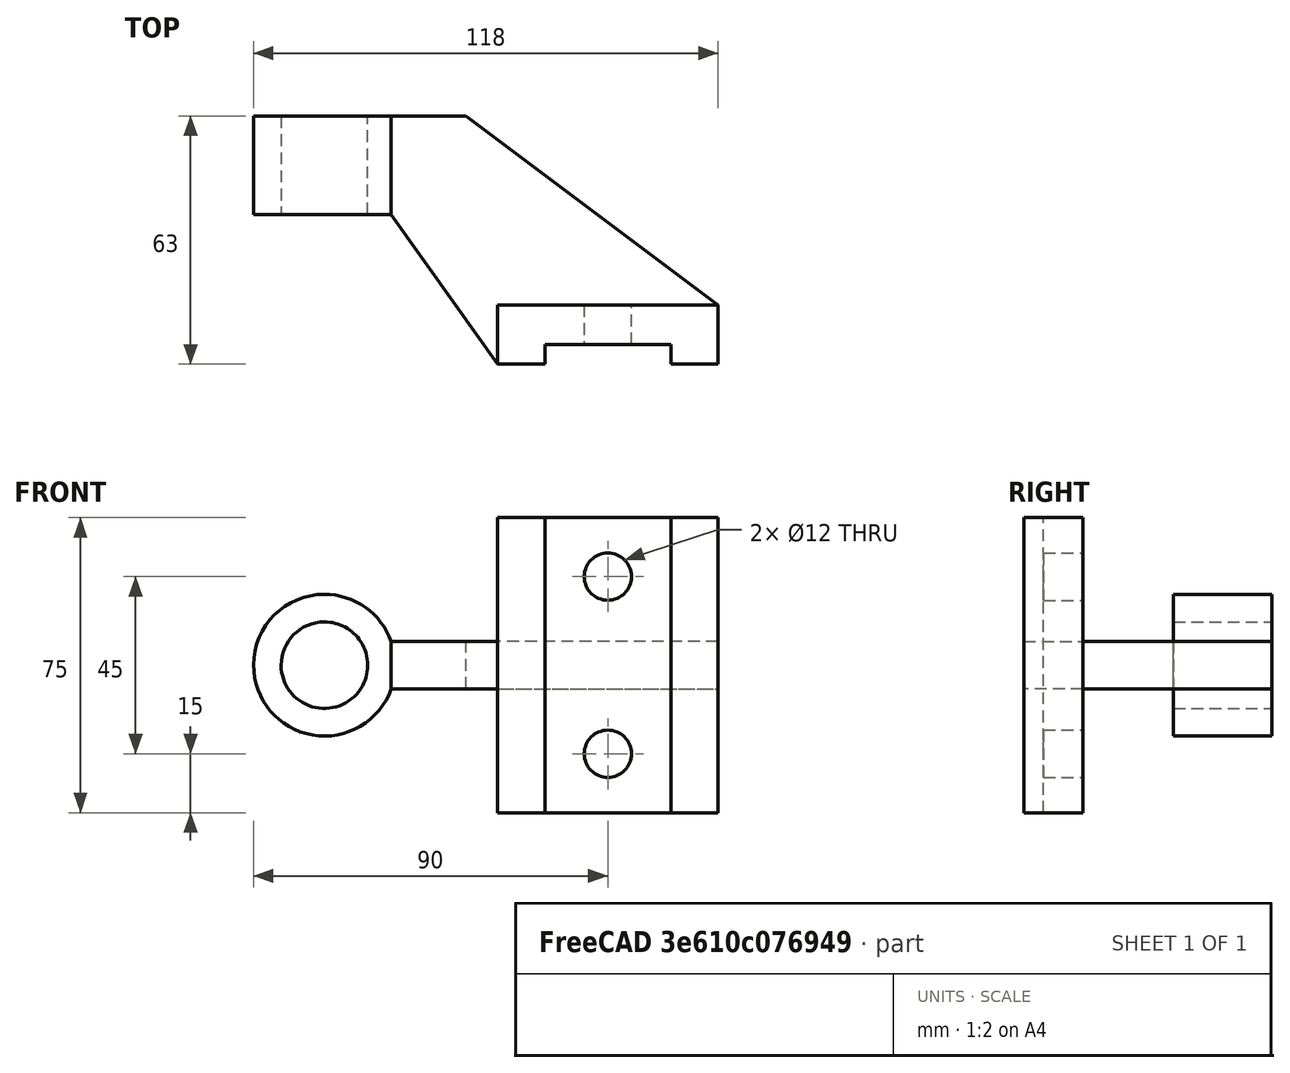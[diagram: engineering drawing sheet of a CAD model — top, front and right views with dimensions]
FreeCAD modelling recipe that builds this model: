
FCSTD DOCUMENT  (FreeCAD 0.18R4 (GitTag))
Label: Ass2 2nd sem
License: All rights reserved
LicenseURL: http://en.wikipedia.org/wiki/All_rights_reserved
objects: TechDraw::DrawViewDimension×15, Sketcher::SketchObject×9, TechDraw::DrawProjGroup×6, PartDesign::Pad×4, PartDesign::Pocket×4, TechDraw::DrawViewAnnotation×3, TechDraw::DrawProjGroupItem×3, TechDraw::DrawSVGTemplate×1, PartDesign::Body×1, TechDraw::DrawPage×1
note: 26 computed .brp shape members not serialized (recipe doc carries the construction recipe); baked Part::Feature solids carry a one-line shape summary decoded from their .brp

FEATURE [Sketcher::SketchObject] Sketch
  MapMode = 5
  Support = -> [XY_Plane]
  sketch-geometry (8):
    g0: LineSegment StartX=-28 StartY=-5.85e-14 StartZ=0 EndX=-28 EndY=15 EndZ=0
    g1: LineSegment StartX=-28 StartY=15 StartZ=0 EndX=28 EndY=15 EndZ=0
    g2: LineSegment StartX=28 StartY=15 StartZ=0 EndX=28 EndY=5.86e-14 EndZ=0
    g3: LineSegment StartX=28 StartY=5.86e-14 StartZ=0 EndX=16 EndY=0 EndZ=0
    g4: LineSegment StartX=16 StartY=0 StartZ=0 EndX=16 EndY=5 EndZ=0
    g5: LineSegment StartX=16 StartY=5 StartZ=0 EndX=-16 EndY=5 EndZ=0
    g6: LineSegment StartX=-16 StartY=5 StartZ=0 EndX=-16 EndY=0 EndZ=0
    g7: LineSegment StartX=-16 StartY=-1e-16 StartZ=0 EndX=-28 EndY=-5.85e-14 EndZ=0
  constraints (23):
    c: Coincident(g0,g1)
    c: Coincident(g1,g2)
    c: Coincident(g2,g3)
    c: Coincident(g3,g4)
    c: Coincident(g4,g5)
    c: Coincident(g5,g6)
    c: Coincident(g6,g7)
    c: Coincident(g7,g0)
    c: Parallel(g7,g3)
    c: Parallel(g3,g5)
    c: Parallel(g5,g1)
    c: DistanceX(g7,g7) = 12
    c: DistanceX(g3,g3) = 12
    c: Parallel(g6,g0)
    c: Parallel(g0,g4)
    c: Parallel(g4,g2)
    c: Parallel(g2,g-2)
    c: DistanceY(g4,g4) = 5
    c: DistanceY(g6,g6) = 5
    c: DistanceY(g2,g2) = 15
    c: Symmetric(g0,g1,g-2)
    c: DistanceX(g1,g1) = 56
    c: PointOnObject(g3,g-1)
FEATURE [PartDesign::Pad] Pad
  Length = 75
  Length2 = 100
  Midplane = true
  Profile = -> Sketch
  Type = 0
FEATURE [Sketcher::SketchObject] Sketch001
  ExternalGeometry = -> [Pad]
  MapMode = 5
  Placement = pos=(0,15,0) rot=(0,0.707107,0.707107;3.14159rad)
  Support = -> [Pad]
  sketch-geometry (4):
    g0: LineSegment StartX=-28 StartY=6 StartZ=0 EndX=72 EndY=6 EndZ=0
    g1: LineSegment StartX=72 StartY=6 StartZ=0 EndX=72 EndY=-6 EndZ=0
    g2: LineSegment StartX=72 StartY=-6 StartZ=0 EndX=-28 EndY=-6 EndZ=0
    g3: LineSegment StartX=-28 StartY=-6 StartZ=0 EndX=-28 EndY=6 EndZ=0
  constraints (11):
    c: Coincident(g0,g1)
    c: Coincident(g1,g2)
    c: Coincident(g2,g3)
    c: Coincident(g3,g0)
    c: Horizontal(g0)
    c: Horizontal(g2)
    c: Vertical(g1)
    c: DistanceY(g3,g3) = 12
    c: PointOnObject(g0,g-3)
    c: Symmetric(g0,g2,g-1)
    c: DistanceX(g0,g0) = 100
FEATURE [PartDesign::Pad] Pad001
  BaseFeature = -> Pad
  Length = 48
  Length2 = 100
  Profile = -> Sketch001
  Type = 0
FEATURE [Sketcher::SketchObject] Sketch002
  ExternalGeometry = -> [Pad001]
  MapMode = 5
  Placement = pos=(0,15,-4.5e-15) rot=(1,0,0;1.5708rad)
  Support = -> [Pad001]
  sketch-geometry (4):
    g0: LineSegment StartX=-28 StartY=6 StartZ=0 EndX=-72 EndY=6 EndZ=0
    g1: LineSegment StartX=-72 StartY=6 StartZ=0 EndX=-72 EndY=-6 EndZ=0
    g2: LineSegment StartX=-72 StartY=-6 StartZ=0 EndX=-28 EndY=-6 EndZ=0
    g3: LineSegment StartX=-28 StartY=-6 StartZ=0 EndX=-28 EndY=6 EndZ=0
  constraints (9):
    c: Coincident(g0,g1)
    c: Coincident(g1,g2)
    c: Coincident(g2,g3)
    c: Coincident(g3,g0)
    c: Horizontal(g2)
    c: Vertical(g1)
    c: Coincident(g2,g-5)
    c: Coincident(g0,g-3)
    c: Coincident(g-3,g0)
FEATURE [PartDesign::Pad] Pad002
  BaseFeature = -> Pad001
  Length = 15
  Length2 = 100
  Profile = -> Sketch002
  Type = 0
FEATURE [Sketcher::SketchObject] Sketch003
  MapMode = 5
  Placement = pos=(0,-1.3e-15,-6) rot=(1,0,0;3.14159rad)
  Support = -> [Pad002]
FEATURE [Sketcher::SketchObject] Sketch004
  ExternalGeometry = -> [Pad002]
  MapMode = 5
  Placement = pos=(0,-1.3e-15,-6) rot=(1,0,0;3.14159rad)
  Support = -> [Pad002]
  sketch-geometry (6):
    g0: LineSegment StartX=-36 StartY=-63 StartZ=0 EndX=28 EndY=-15 EndZ=0
    g1: LineSegment StartX=28 StartY=-15 StartZ=0 EndX=28 EndY=-63 EndZ=0
    g2: LineSegment StartX=28 StartY=-63 StartZ=0 EndX=-36 EndY=-63 EndZ=0
    g3: LineSegment StartX=-72 StartY=-38 StartZ=0 EndX=-28 EndY=4.97e-14 EndZ=0
    g4: LineSegment StartX=-28 StartY=4.97e-14 StartZ=0 EndX=-72 EndY=-5.86e-14 EndZ=0
    g5: LineSegment StartX=-72 StartY=-5.86e-14 StartZ=0 EndX=-72 EndY=-38 EndZ=0
  constraints (10):
    c: Coincident(g0,g1)
    c: Coincident(g1,g2)
    c: Coincident(g2,g0)
    c: Coincident(g1,g-3)
    c: Coincident(g0,g-5)
    c: Coincident(g3,g4)
    c: Coincident(g4,g5)
    c: Coincident(g5,g3)
    c: Coincident(g4,g-7)
    c: Coincident(g3,g-6)
FEATURE [PartDesign::Pocket] Pocket
  BaseFeature = -> Pad002
  Length = 5
  Length2 = 100
  Profile = -> Sketch004
  Type = 1
FEATURE [Sketcher::SketchObject] Sketch005
  ExternalGeometry = -> [Pocket]
  MapMode = 5
  Placement = pos=(0,63,-1.89e-14) rot=(0,0.707107,0.707107;3.14159rad)
  Support = -> [Pocket]
  sketch-geometry (2):
    g0: Circle CenterX=72 CenterY=0 CenterZ=0 NormalX=0 NormalY=0 NormalZ=1 AngleXU=0 Radius=18
    g1: Circle CenterX=72 CenterY=0 CenterZ=0 NormalX=0 NormalY=0 NormalZ=1 AngleXU=0 Radius=11
  constraints (5):
    c: Radius(g0) = 18
    c: PointOnObject(g0,g-3)
    c: PointOnObject(g0,g-1)
    c: Radius(g1) = 11
    c: Coincident(g1,g0)
FEATURE [Sketcher::SketchObject] Sketch007
  MapMode = 5
  Placement = pos=(0,15,0) rot=(0,0.707107,0.707107;3.14159rad)
  sketch-geometry (2):
    g0: Circle CenterX=0 CenterY=22.5 CenterZ=0 NormalX=0 NormalY=0 NormalZ=1 AngleXU=0 Radius=6
    g1: Circle CenterX=0 CenterY=-22.5 CenterZ=0 NormalX=0 NormalY=0 NormalZ=1 AngleXU=0 Radius=6
  constraints (5):
    c: PointOnObject(g1,g-2)
    c: PointOnObject(g0,g-2)
    c: Radius(g0) = 6
    c: Radius(g1) = 6
    c: DistanceY(g1,g0) = 45
FEATURE [PartDesign::Pocket] Pocket002
  BaseFeature = -> Pocket
  Length = 5
  Length2 = 100
  Profile = -> Sketch007
  Type = 1
FEATURE [TechDraw::DrawSVGTemplate] Template
  EditableTexts = Designed_by_Name=Soumojit Shome; Drawing_number=Assignment 2; FC-Date=21/04/2023; FC-SC=1:1; FC-SH=02; FC-Title=Academy of Technology; Subtitle=ECE2 (Y) 16900322101; Weight=Weight
  Height = 210
  Orientation = 1
  Width = 297
FEATURE [TechDraw::DrawProjGroup] ProjGroup
  AutoDistribute = true
  LockPosition = false
  ProjectionType = 0
  Rotation = 0
  ScaleType = 0
  Source = -> [Pocket002]
  X = 87.9071
  Y = 164.348
  spacingX = 15
  spacingY = 15
FEATURE [TechDraw::DrawViewAnnotation] Annotation
  Font = osifont
  LineSpace = 80
  LockPosition = false
  MaxWidth = -1
  Rotation = 0
  ScaleType = 0
  Text = Front View
  TextSize = 8
  TextStyle = 0
  X = 139.37
  Y = 143.597
FEATURE [TechDraw::DrawProjGroup] ProjGroup001
  AutoDistribute = true
  LockPosition = false
  ProjectionType = 0
  Rotation = 0
  ScaleType = 0
  Source = -> [Pocket002]
  X = 87.9071
  Y = 82.1739
  spacingX = 15
  spacingY = 15
FEATURE [TechDraw::DrawProjGroup] ProjGroup002
  AutoDistribute = true
  LockPosition = false
  ProjectionType = 0
  Rotation = 0
  ScaleType = 0
  Source = -> [Pocket002]
  X = 221.958
  Y = 135.296
  spacingX = 15
  spacingY = 15
FEATURE [TechDraw::DrawViewAnnotation] Annotation001
  Font = osifont
  LineSpace = 80
  LockPosition = false
  MaxWidth = -1
  Rotation = 0
  ScaleType = 0
  Text = Top View
  TextSize = 8
  TextStyle = 0
  X = 91.2273
  Y = 19.0909
FEATURE [TechDraw::DrawViewAnnotation] Annotation002
  Font = osifont
  LineSpace = 80
  LockPosition = false
  MaxWidth = -1
  Rotation = 0
  ScaleType = 0
  Text = Isometric View
  TextSize = 8
  TextStyle = 0
  X = 226.109
  Y = 70.9684
FEATURE [PartDesign::Pad] Pad003
  BaseFeature = -> Pocket002
  Length = 25
  Length2 = 100
  Profile = -> Sketch005
  Reversed = true
  Type = 0
FEATURE [Sketcher::SketchObject] Sketch008
  ExternalGeometry = -> [Pad003]
  MapMode = 5
  Placement = pos=(0,-1.3e-15,-6) rot=(1,0,0;3.14159rad)
  Support = -> [Pad003]
  sketch-geometry (3):
    g0: LineSegment StartX=-28 StartY=4.97e-14 StartZ=0 EndX=-55.0294 EndY=-38 EndZ=0
    g1: LineSegment StartX=-55.0294 StartY=-38 StartZ=0 EndX=-72 EndY=-38 EndZ=0
    g2: LineSegment StartX=-72 StartY=-38 StartZ=0 EndX=-28 EndY=4.97e-14 EndZ=0
  constraints (6):
    c: Coincident(g0,g1)
    c: Coincident(g1,g2)
    c: Coincident(g2,g0)
    c: Coincident(g2,g-4)
    c: Coincident(g0,g-3)
    c: Coincident(g1,g-5)
FEATURE [PartDesign::Pocket] Pocket003
  BaseFeature = -> Pad003
  Length = 5
  Length2 = 100
  Profile = -> Sketch008
  Type = 1
FEATURE [Sketcher::SketchObject] Sketch009
  ExternalGeometry = -> [Pocket003]
  MapMode = 5
  Placement = pos=(0,63,-1.89e-14) rot=(0,0.707107,0.707107;3.14159rad)
  Support = -> [Pocket003]
  sketch-geometry (4):
    g0: ArcOfCircle CenterX=72 CenterY=-8e-16 CenterZ=0 NormalX=0 NormalY=0 NormalZ=1 AngleXU=0 Radius=11 StartAngle=2.56466 EndAngle=3.71852
    g1: LineSegment StartX=62.7805 StartY=6 StartZ=0 EndX=72 EndY=6 EndZ=0
    g2: LineSegment StartX=72 StartY=6 StartZ=0 EndX=72 EndY=-6 EndZ=0
    g3: LineSegment StartX=72 StartY=-6 StartZ=0 EndX=62.7805 EndY=-6 EndZ=0
  constraints (9):
    c: Coincident(g0,g-3)
    c: Coincident(g0,g-3)
    c: Coincident(g0,g-3)
    c: Coincident(g1,g2)
    c: Coincident(g2,g3)
    c: Coincident(g3,g0)
    c: Coincident(g1,g0)
    c: Coincident(g1,g-4)
    c: Coincident(g-4,g2)
FEATURE [PartDesign::Pocket] Pocket004
  BaseFeature = -> Pocket003
  Length = 5
  Length2 = 100
  Profile = -> Sketch009
  Type = 1
FEATURE [PartDesign::Body] Body
  Group = -> [Sketch,Pad,Sketch001,Pad001,Sketch002,Pad002,Sketch003,Sketch004,Pocket,Sketch005,Sketch007,Pocket002,Pad003,Sketch008,Pocket003,Sketch009,Pocket004]
  Origin = -> Origin
  Tip = -> Pocket004
FEATURE [TechDraw::DrawProjGroupItem] ProjItem  label="Front"
  CoarseView = false
  Direction = (0,0,-1)
  Focus = 100
  HardHidden = false
  IsoCount = 0
  IsoHidden = false
  IsoVisible = false
  LockPosition = true
  Perspective = false
  Rotation = 0
  RotationVector = (-1,0,0)
  ScaleType = 2
  SeamHidden = false
  SeamVisible = false
  SmoothHidden = false
  SmoothVisible = false
  Source = -> [Pocket004]
  Type = 0
  X = 0
  Y = 0
FEATURE [TechDraw::DrawProjGroup] ProjGroup003
  Anchor = -> ProjItem
  AutoDistribute = true
  LockPosition = false
  ProjectionType = 0
  Rotation = 0
  ScaleType = 0
  Source = -> [Pocket004]
  Views = -> [ProjItem]
  X = 86.247
  Y = 164.763
  spacingX = 15
  spacingY = 15
FEATURE [TechDraw::DrawProjGroupItem] ProjItem001  label="Front001"
  CoarseView = false
  Direction = (0,1,0)
  Focus = 100
  HardHidden = false
  IsoCount = 0
  IsoHidden = false
  IsoVisible = false
  LockPosition = true
  Perspective = false
  Rotation = 0
  RotationVector = (-1,0,0)
  ScaleType = 2
  SeamHidden = false
  SeamVisible = false
  SmoothHidden = false
  SmoothVisible = false
  Source = -> [Pocket004]
  Type = 0
  X = 0
  Y = 0
FEATURE [TechDraw::DrawProjGroup] ProjGroup004
  Anchor = -> ProjItem001
  AutoDistribute = true
  LockPosition = false
  ProjectionType = 0
  Rotation = 0
  ScaleType = 0
  Source = -> [Pocket004]
  Views = -> [ProjItem001]
  X = 94.5474
  Y = 73.8735
  spacingX = 15
  spacingY = 15
FEATURE [TechDraw::DrawProjGroupItem] ProjItem002  label="Front002"
  CoarseView = false
  Direction = (0.715,0.437,-0.546)
  Focus = 100
  HardHidden = false
  IsoCount = 0
  IsoHidden = false
  IsoVisible = false
  LockPosition = true
  Perspective = false
  Rotation = 0
  RotationVector = (-0.623,0.042,-0.781)
  ScaleType = 2
  SeamHidden = false
  SeamVisible = false
  SmoothHidden = false
  SmoothVisible = false
  Source = -> [Pocket004]
  Type = 0
  X = 0
  Y = 0
FEATURE [TechDraw::DrawProjGroup] ProjGroup005
  Anchor = -> ProjItem002
  AutoDistribute = true
  LockPosition = false
  ProjectionType = 0
  Rotation = 0
  ScaleType = 0
  Source = -> [Pocket004]
  Views = -> [ProjItem002]
  X = 215.318
  Y = 134.881
  spacingX = 15
  spacingY = 15
FEATURE [TechDraw::DrawViewDimension] Dimension
  Arbitrary = false
  FormatSpec = ⌀%.2f
  LockPosition = false
  MeasureType = 1
  OverTolerance = 0
  References2D = -> [ProjItem001]
  Rotation = 0
  ScaleType = 0
  Type = 5
  UnderTolerance = 0
  X = 26.9763
  Y = 34.8617
FEATURE [TechDraw::DrawViewDimension] Dimension001
  Arbitrary = false
  FormatSpec = ⌀%.2f
  LockPosition = false
  MeasureType = 1
  OverTolerance = 0
  References2D = -> [ProjItem001]
  Rotation = 0
  ScaleType = 0
  Type = 5
  UnderTolerance = 0
  X = 18.2609
  Y = 24.4862
FEATURE [TechDraw::DrawViewDimension] Dimension002
  Arbitrary = false
  FormatSpec = %.2f
  LockPosition = false
  MeasureType = 1
  OverTolerance = 0
  References2D = -> [ProjItem]
  Rotation = 0
  ScaleType = 0
  Type = 2
  UnderTolerance = 0
  X = 63.5652
  Y = 19
FEATURE [TechDraw::DrawViewDimension] Dimension003
  Arbitrary = false
  FormatSpec = %.2f
  LockPosition = false
  MeasureType = 1
  OverTolerance = 0
  References2D = -> [ProjItem001]
  Rotation = 0
  ScaleType = 0
  Type = 1
  UnderTolerance = 0
  X = 22.585
  Y = -22.5059
FEATURE [TechDraw::DrawViewDimension] Dimension004
  Arbitrary = false
  FormatSpec = %.2f
  LockPosition = false
  MeasureType = 1
  OverTolerance = 0
  References2D = -> [ProjItem001]
  Rotation = 0
  ScaleType = 0
  Type = 1
  UnderTolerance = 0
  X = -6.9249
  Y = -41.1818
FEATURE [TechDraw::DrawViewDimension] Dimension005
  Arbitrary = false
  FormatSpec = %.2f
  LockPosition = false
  MeasureType = 1
  OverTolerance = 0
  References2D = -> [ProjItem001]
  Rotation = 0
  ScaleType = 0
  Type = 1
  UnderTolerance = 0
  X = -45
  Y = -52.8261
FEATURE [TechDraw::DrawViewDimension] Dimension006
  Arbitrary = false
  FormatSpec = %.2f
  LockPosition = false
  MeasureType = 1
  OverTolerance = 0
  References2D = -> [ProjItem001]
  Rotation = 0
  ScaleType = 0
  Type = 2
  UnderTolerance = 0
  X = -67.3004
  Y = 1.66008
FEATURE [TechDraw::DrawViewDimension] Dimension007
  Arbitrary = false
  FormatSpec = %.2f
  LockPosition = false
  MeasureType = 1
  OverTolerance = 0
  References2D = -> [ProjItem001]
  Rotation = 0
  ScaleType = 0
  Type = 2
  UnderTolerance = 0
  X = -75.4071
  Y = -4.1502
FEATURE [TechDraw::DrawViewDimension] Dimension008
  Arbitrary = false
  FormatSpec = %.2f
  LockPosition = false
  MeasureType = 1
  OverTolerance = 0
  References2D = -> [ProjItem001]
  Rotation = 0
  ScaleType = 0
  Type = 2
  UnderTolerance = 0
  X = -80.996
  Y = 17.8458
FEATURE [TechDraw::DrawViewDimension] Dimension009
  Arbitrary = false
  FormatSpec = %.2f
  LockPosition = false
  MeasureType = 1
  OverTolerance = 0
  References2D = -> [ProjItem]
  Rotation = 0
  ScaleType = 0
  Type = 1
  UnderTolerance = 0
  X = -44.6996
  Y = -36.4802
FEATURE [TechDraw::DrawViewDimension] Dimension010
  Arbitrary = false
  FormatSpec = %.2f
  LockPosition = false
  MeasureType = 1
  OverTolerance = 0
  References2D = -> [ProjItem]
  Rotation = 0
  ScaleType = 0
  Type = 1
  UnderTolerance = 0
  X = -28.5099
  Y = -42.7055
FEATURE [TechDraw::DrawViewDimension] Dimension011
  Arbitrary = false
  FormatSpec = %.2f
  LockPosition = false
  MeasureType = 1
  OverTolerance = 0
  References2D = -> [ProjItem]
  Rotation = 0
  ScaleType = 0
  Type = 2
  UnderTolerance = 0
  X = 19.8182
  Y = -15.3043
FEATURE [TechDraw::DrawViewDimension] Dimension012
  Arbitrary = false
  FormatSpec = %.2f
  LockPosition = false
  MeasureType = 1
  OverTolerance = 0
  References2D = -> [ProjItem]
  Rotation = 0
  ScaleType = 0
  Type = 2
  UnderTolerance = 0
  X = -72.6957
  Y = -19.0198
FEATURE [TechDraw::DrawViewDimension] Dimension013
  Arbitrary = false
  FormatSpec = ⌀%.2f
  LockPosition = false
  MeasureType = 1
  OverTolerance = 0
  References2D = -> [ProjItem001]
  Rotation = 0
  ScaleType = 0
  Type = 5
  UnderTolerance = 0
  X = -15.3557
  Y = 12.0356
FEATURE [TechDraw::DrawViewDimension] Dimension014
  Arbitrary = false
  FormatSpec = %.2f
  LockPosition = false
  MeasureType = 1
  OverTolerance = 0
  References2D = -> [ProjItem]
  Rotation = 0
  ScaleType = 0
  Type = 2
  UnderTolerance = 0
  X = -67.4822
  Y = 7.88538
FEATURE [TechDraw::DrawPage] Page
  KeepUpdated = true
  ProjectionType = 0
  Template = -> Template
  Views = -> [ProjGroup,Annotation,ProjGroup001,ProjGroup002,Annotation001,Annotation002,ProjGroup003,ProjGroup004,ProjGroup005,Dimension,Dimension001,Dimension002,Dimension003,Dimension004,Dimension005,Dimension006,Dimension007,Dimension008,Dimension009,Dimension010,Dimension011,Dimension012,Dimension013,Dimension014]
